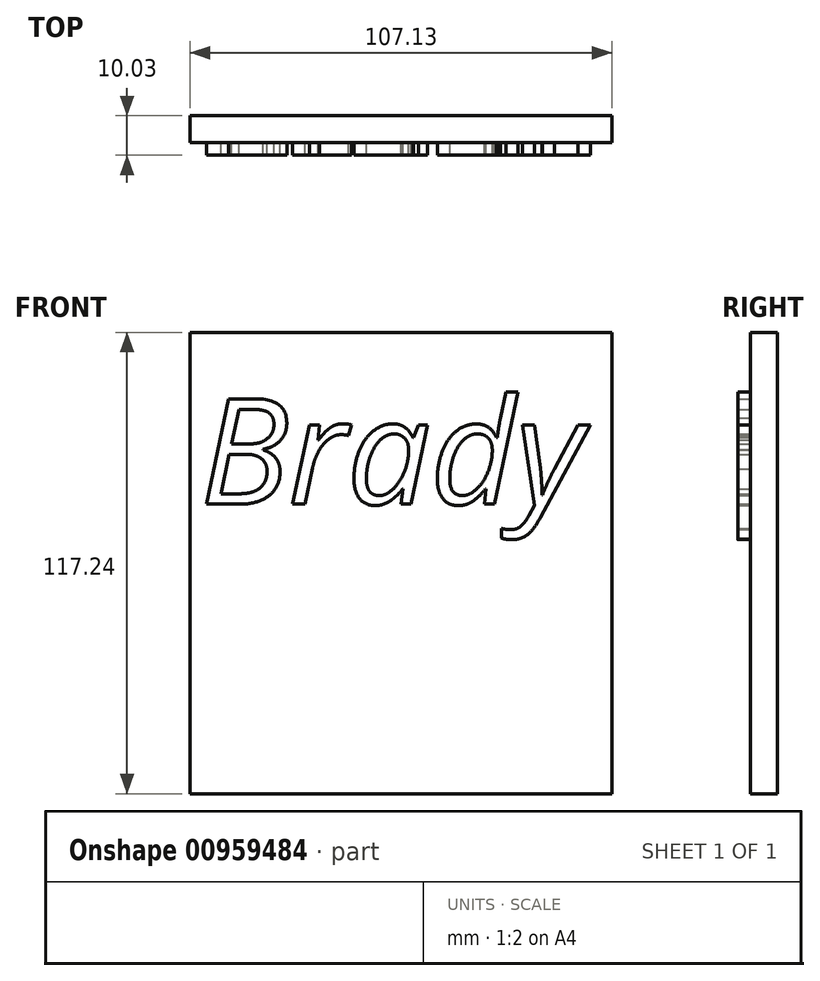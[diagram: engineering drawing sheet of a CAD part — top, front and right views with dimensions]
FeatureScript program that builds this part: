
annotation { "Feature Type Name" : "Feature", "Feature Type Description" : "" }
export const myFeature = defineFeature(function(context is Context, id is Id, definition is map)
    precondition{}
    {
        {
            var Q0;
            Q0=qCreatedBy(makeId("Front.planeOp"),FACE);
            var sketch = newSketch(context, id + "F0", { "sketchPlane" : qUnion([Q0])});
            skLineSegment(sketch, "E0.bottom", {"start": v(-46.02, 68.74) * mm, "end": v(61.11, 68.74) * mm});
            skLineSegment(sketch, "E0.top", {"start": v(-46.02, -48.5) * mm, "end": v(61.11, -48.5) * mm});
            skLineSegment(sketch, "E0.left", {"start": v(-46.02, 68.74) * mm, "end": v(-46.02, -48.5) * mm});
            skLineSegment(sketch, "E0.right", {"start": v(61.11, 68.74) * mm, "end": v(61.11, -48.5) * mm});
            skSolve(sketch);
        }
        {
            var Q0;
            Q0 = qSketchRegion(id + "F0", true);
            var Q1;
            Q1=makeQuery(id+"F0.imprint","IMPRINT",FACE,{"disambiguationData":[TD([[makeQuery(id+"F0.imprint","IMPRINT",EDGE,{"derivedFrom":sQuery(id+"F0.wireOp",EDGE,"c43ef49b-6605-4f33-8a01-1aeb8f09d2f9.sketch_text.stroke-26")}),1.0]])]});
            var Q2;
            Q2=makeQuery(id+"F0.imprint","IMPRINT",FACE,{"disambiguationData":[TD([[makeQuery(id+"F0.imprint","IMPRINT",EDGE,{"derivedFrom":sQuery(id+"F0.wireOp",EDGE,"c43ef49b-6605-4f33-8a01-1aeb8f09d2f9.sketch_text.stroke-51")}),1.0]])]});
            var Q3;
            Q3=makeQuery(id+"F0.imprint","IMPRINT",FACE,{"disambiguationData":[TD([[makeQuery(id+"F0.imprint","IMPRINT",EDGE,{"derivedFrom":sQuery(id+"F0.wireOp",EDGE,"c43ef49b-6605-4f33-8a01-1aeb8f09d2f9.sketch_text.stroke-92")}),1.0]])]});
            extrude(context, id + "F1", {"entities" : qUnion([Q0, Q1, Q2, Q3]), "depth" : 6.86 * mm, "offsetDistance" : 25.4 * mm});
        }
        {
            var Q0;
            Q0=makeQuery(id+"F1.opExtrude","CAP_FACE",FACE,{"disambiguationData":[OSD([sQuery(id+"F0.wireOp",EDGE,"E0.bottom"),sQuery(id+"F0.wireOp",EDGE,"E0.top"),sQuery(id+"F0.wireOp",EDGE,"E0.left"),sQuery(id+"F0.wireOp",EDGE,"E0.right")])],"isStart":false});
            var sketch = newSketch(context, id + "F2", { "sketchPlane" : qUnion([Q0])});
            skText(sketch, "E1", { "text": "Brady", "fontName": "OpenSans-Italic.ttf"});
            const initialGuessF2  = {"E1": [-0.04348, 0.02507, 1, 0, 0.027]};
            skSetInitialGuess(sketch, initialGuessF2);
            skSolve(sketch);
        }
        {
            var Q0;
            Q0 = qSketchRegion(id + "F2", true);
            extrude(context, id + "F3", {"entities" : qUnion([Q0]), "operationType" : NewBodyOperationType.ADD, "depth" : 3.17 * mm, "offsetDistance" : 25.4 * mm});
        }
    });
